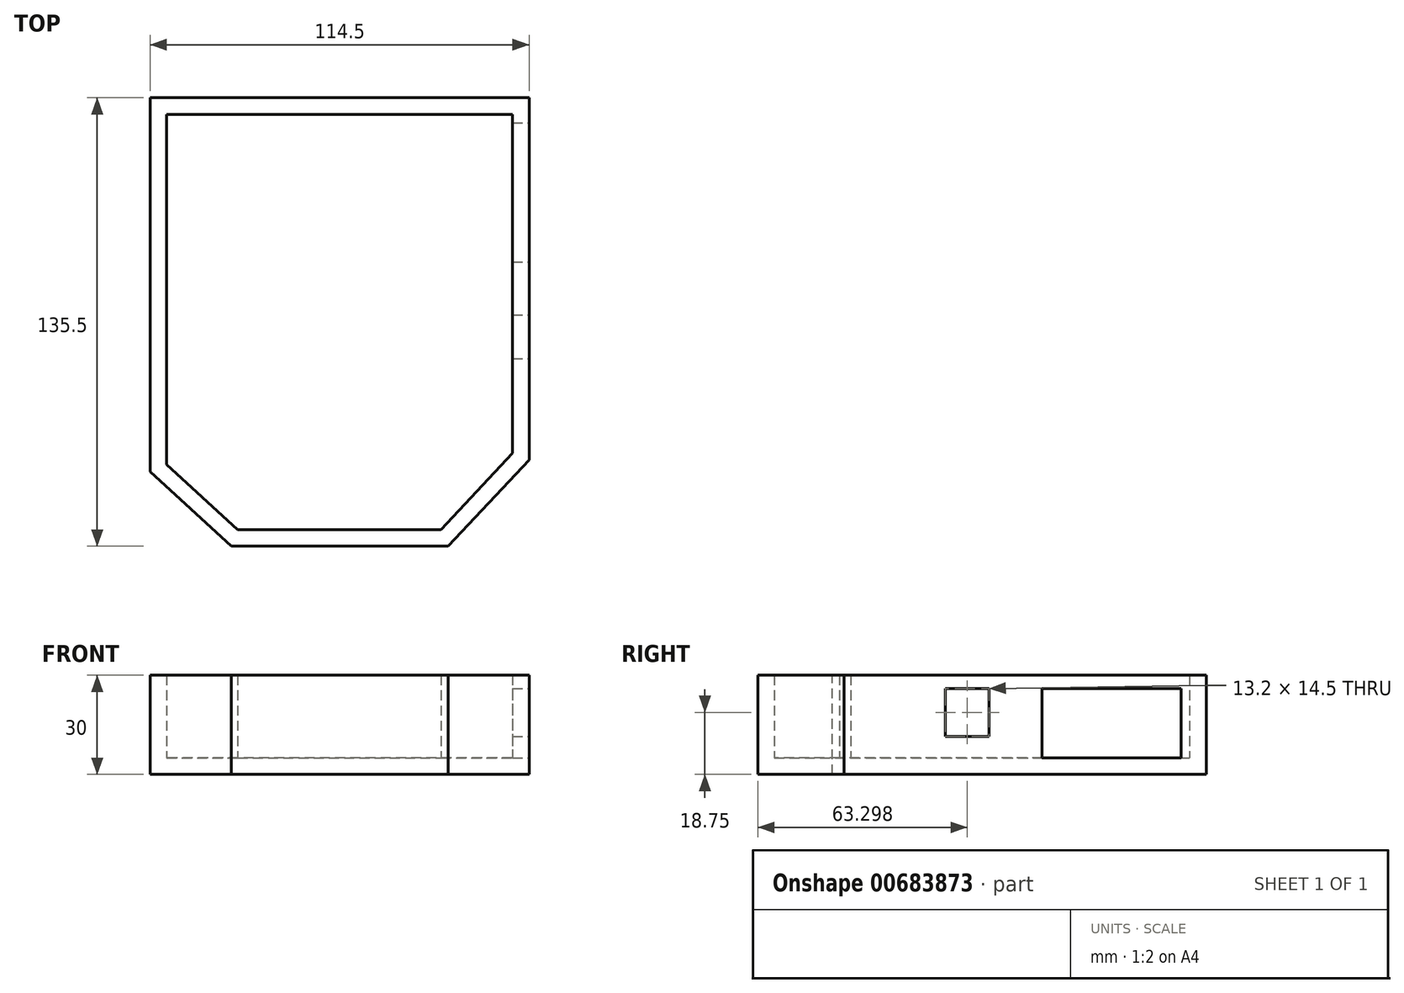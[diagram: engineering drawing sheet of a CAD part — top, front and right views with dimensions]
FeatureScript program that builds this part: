
annotation { "Feature Type Name" : "Feature", "Feature Type Description" : "" }
export const myFeature = defineFeature(function(context is Context, id is Id, definition is map)
    precondition{}
    {
        {
            var Q0;
            Q0=qCreatedBy(makeId("Top.planeOp"),FACE);
            var sketch = newSketch(context, id + "F0", { "sketchPlane" : qUnion([Q0])});
            skLineSegment(sketch, "E0.bottom", {"start": v(-85.83, 123.18) * mm, "end": v(28.67, 123.18) * mm});
            skLineSegment(sketch, "E0.top", {"start": v(-61.33, -12.32) * mm, "end": v(4.17, -12.32) * mm});
            skLineSegment(sketch, "E0.left", {"start": v(-85.83, 123.18) * mm, "end": v(-85.83, 10.18) * mm});
            skLineSegment(sketch, "E0.right", {"start": v(28.67, 123.18) * mm, "end": v(28.67, 13.77) * mm});
            skLineSegment(sketch, "E1", {"start": v(-85.83, 10.18) * mm, "end": v(-61.33, -12.32) * mm});
            skLineSegment(sketch, "E2", {"start": v(4.17, -12.32) * mm, "end": v(28.67, 13.77) * mm});
            skPoint(sketch, "E3.orphan", {"position": v(-85.83, -12.32) * mm});
            skPoint(sketch, "E4.orphan", {"position": v(28.67, -12.32) * mm});
            skSolve(sketch);
        }
        {
            var Q0;
            {var subQ1=sQuery(id+"F0.wireOp",EDGE,"E0.bottom");Q0=makeQuery(id+"F0.imprint","IMPRINT",FACE,{"disambiguationData":[TD([[makeQuery(id+"F0.imprint","IMPRINT",EDGE,{"derivedFrom":subQ1}),-1.0]])]});}
            var sketch = newSketch(context, id + "F1", { "sketchPlane" : qUnion([Q0])});
            skSolve(sketch);
        }
        {
            var Q0;
            Q0 = qSketchRegion(id + "F0", true);
            extrude(context, id + "F2", {"entities" : qUnion([Q0]), "oppositeDirection" : true, "depth" : 5 * mm, "offsetDistance" : 25 * mm});
        }
        {
            var Q0;
            Q0=makeQuery(id+"F1.imprint","IMPRINT",FACE,{"disambiguationData":[TD([[makeQuery(id+"F1.imprint","IMPRINT",EDGE,{"derivedFrom":makeQuery(id+"F0.imprint","IMPRINT",EDGE,{"derivedFrom":sQuery(id+"F0.wireOp",EDGE,"E0.bottom")})}),-1.0]])]});
            var sketch = newSketch(context, id + "F3", { "sketchPlane" : qUnion([Q0])});
            skLineSegment(sketch, "E5.0", {"start": v(23.67, 118.18) * mm, "end": v(-80.83, 118.18) * mm});
            skLineSegment(sketch, "E5.1", {"start": v(-80.83, 12.37) * mm, "end": v(-59.38, -7.32) * mm});
            skLineSegment(sketch, "E5.2", {"start": v(-59.38, -7.32) * mm, "end": v(2, -7.32) * mm});
            skLineSegment(sketch, "E5.3", {"start": v(-80.83, 118.18) * mm, "end": v(-80.83, 12.37) * mm});
            skLineSegment(sketch, "E5.4", {"start": v(2, -7.32) * mm, "end": v(23.67, 15.75) * mm});
            skLineSegment(sketch, "E5.5", {"start": v(23.67, 15.75) * mm, "end": v(23.67, 118.18) * mm});
            skSolve(sketch);
        }
        {
            var Q0;
            Q0=makeQuery(id+"F3.imprint","IMPRINT",FACE,{"disambiguationData":[TD([[makeQuery(id+"F3.imprint","IMPRINT",EDGE,{"derivedFrom":sQuery(id+"F3.wireOp",EDGE,"E5.0")}),-1.0]])]});
            extrude(context, id + "F4", {"entities" : qUnion([Q0]), "operationType" : NewBodyOperationType.ADD, "depth" : 25 * mm, "offsetDistance" : 25 * mm});
        }
        {
            var Q0;
            {var subQ0=sQuery(id+"F0.wireOp",EDGE,"E0.right");Q0=makeQuery(id+"F4.boolean.opBoolean","MERGE",FACE,{"derivedFrom":[makeQuery(id+"F2.opExtrude","SWEPT_FACE",FACE,{"disambiguationData":[OSD([subQ0])]}),makeQuery(id+"F4.opExtrude","SWEPT_FACE",FACE,{"disambiguationData":[OSD([subQ0])]})]});}
            var sketch = newSketch(context, id + "F5", { "sketchPlane" : qUnion([Q0])});
            skLineSegment(sketch, "E6.bottom", {"start": v(73.58, 21) * mm, "end": v(115.58, 21) * mm});
            skLineSegment(sketch, "E6.top", {"start": v(73.58, 0) * mm, "end": v(115.58, 0) * mm});
            skLineSegment(sketch, "E6.left", {"start": v(73.58, 21) * mm, "end": v(73.58, 0) * mm});
            skLineSegment(sketch, "E6.right", {"start": v(115.58, 21) * mm, "end": v(115.58, 0) * mm});
            skLineSegment(sketch, "E7.bottom", {"start": v(57.58, 21) * mm, "end": v(44.38, 21) * mm});
            skLineSegment(sketch, "E7.top", {"start": v(57.58, 6.5) * mm, "end": v(44.38, 6.5) * mm});
            skLineSegment(sketch, "E7.left", {"start": v(57.58, 21) * mm, "end": v(57.58, 6.5) * mm});
            skLineSegment(sketch, "E7.right", {"start": v(44.38, 21) * mm, "end": v(44.38, 6.5) * mm});
            skSolve(sketch);
        }
        {
            var Q0;
            Q0=makeQuery(id+"F5.imprint","IMPRINT",FACE,{"disambiguationData":[TD([[makeQuery(id+"F5.imprint","IMPRINT",EDGE,{"derivedFrom":sQuery(id+"F5.wireOp",EDGE,"E6.bottom")}),-1.0]])]});
            var Q1;
            Q1=makeQuery(id+"F5.imprint","IMPRINT",FACE,{"disambiguationData":[TD([[makeQuery(id+"F5.imprint","IMPRINT",EDGE,{"derivedFrom":sQuery(id+"F5.wireOp",EDGE,"E7.bottom")}),1.0]])]});
            extrude(context, id + "F6", {"entities" : qUnion([Q0, Q1]), "operationType" : NewBodyOperationType.REMOVE, "depth" : 5 * mm, "offsetDistance" : 25 * mm});
        }
        {
            var Q0;
            Q0=makeQuery(id+"F5.imprint","IMPRINT",FACE,{"disambiguationData":[TD([[makeQuery(id+"F5.imprint","IMPRINT",EDGE,{"derivedFrom":sQuery(id+"F5.wireOp",EDGE,"E6.bottom")}),-1.0]])]});
            var Q1;
            Q1=makeQuery(id+"F5.imprint","IMPRINT",FACE,{"disambiguationData":[TD([[makeQuery(id+"F5.imprint","IMPRINT",EDGE,{"derivedFrom":sQuery(id+"F5.wireOp",EDGE,"E7.bottom")}),1.0]])]});
            extrude(context, id + "F7", {"entities" : qUnion([Q0, Q1]), "operationType" : NewBodyOperationType.REMOVE, "endBound" : BoundingType.UP_TO_NEXT, "oppositeDirection" : true, "depth" : 25 * mm, "offsetDistance" : 25 * mm});
        }
    });
